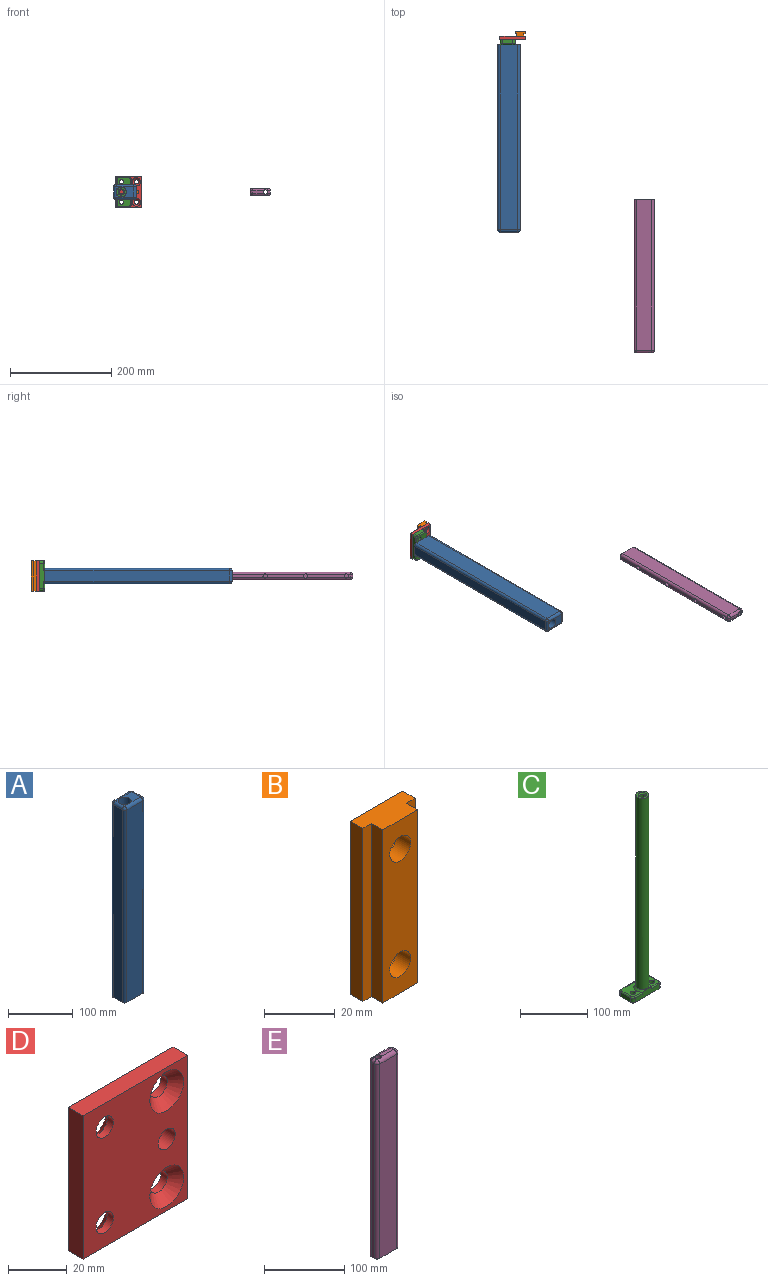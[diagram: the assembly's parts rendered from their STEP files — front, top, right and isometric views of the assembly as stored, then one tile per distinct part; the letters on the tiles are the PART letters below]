
ASSEMBLY  parts=5 mates=9
PART A: 32 faces, bbox 45x30x370 mm
  f0: plane 8.58x8.58mm, normal (0,0,1), area 20.1mm2, adj f6,f27,f31
  f1: plane 8.58x8.58mm, normal (0,0,1), area 20.1mm2, adj f6,f28,f31
  f2: plane 365x20mm, normal (-1,0,0), area 7300mm2, adj f8,f9,f12,f31
  f3: plane 365x35mm, normal (0,-1,0), area 12775mm2, adj f8,f9,f10,f27
  f4: plane 365x20mm, normal (1,0,0), area 7022.9mm2, adj f8,f10,f11,f13,f15,f17,f19,f21
  f5: plane 365x35mm, normal (0,1,0), area 12775mm2, adj f8,f11,f12,f28
  f6: cylinder r=10.1mm len=363mm, axis (0,0,-1), area 23036mm2, adj f0,f1,f7,f23,f27,f28,f31
  f7: plane 23.58x20mm, normal (0,0,1), area 340mm2, adj f6,f24,f27,f28
  f8: plane 45x30mm, normal (0,0,-1), area 868.6mm2, adj f2,f3,f4,f5,f9,f10,f11,f12
  f9: cylinder r=5mm len=365mm, axis (0,0,1), area 2866.7mm2, adj f2,f3,f8,f29
  f10: cylinder r=5mm len=365mm, axis (0,0,-1), area 2866.7mm2, adj f3,f4,f8,f25
  f11: cylinder r=5mm len=365mm, axis (0,0,1), area 2866.7mm2, adj f4,f5,f8,f26
  f12: cylinder r=5mm len=365mm, axis (0,0,-1), area 2866.7mm2, adj f2,f5,f8,f30
  f13: cylinder r=4.2mm len=15mm, axis (1,0,0), area 395.8mm2, adj f4,f14
  f14: plane 8.4x8.4mm, normal (1,0,0), area 55.4mm2, adj f13
  f15: cylinder r=4.2mm len=15mm, axis (1,0,0), area 395.8mm2, adj f4,f16
  f16: plane 8.4x8.4mm, normal (1,0,0), area 55.4mm2, adj f15
  f17: cylinder r=4.2mm len=15mm, axis (1,0,0), area 395.8mm2, adj f4,f18
  f18: plane 8.4x8.4mm, normal (1,0,0), area 55.4mm2, adj f17
  f19: cylinder r=4.2mm len=15mm, axis (1,0,0), area 395.8mm2, adj f4,f20
  f20: plane 8.4x8.4mm, normal (1,0,0), area 55.4mm2, adj f19
  f21: cylinder r=4.2mm len=15mm, axis (1,0,0), area 395.8mm2, adj f4,f22
  f22: plane 8.4x8.4mm, normal (1,0,0), area 55.4mm2, adj f21
  f23: cone r=12.1mm half-angle=15.9deg, axis (0,0,-1), area 507.7mm2, adj f6,f8
  f24: cylinder r=5mm len=20mm, axis (0,-1,0), area 157.1mm2, adj f4,f7,f25,f26
  f25: sphere r=5mm, area 39.3mm2, adj f10,f24,f27
  f26: sphere r=5mm, area 39.3mm2, adj f11,f24,f28
  f27: cylinder r=5mm len=35mm, axis (-1,0,0), area 274.7mm2, adj f0,f3,f6,f7,f25,f29
  f28: cylinder r=5mm len=35mm, axis (1,0,0), area 274.7mm2, adj f1,f5,f6,f7,f26,f30
  f29: sphere r=5mm, area 39.3mm2, adj f9,f27,f31
  f30: sphere r=5mm, area 39.3mm2, adj f12,f28,f31
  f31: cylinder r=5mm len=20mm, axis (0,1,0), area 156.9mm2, adj f0,f1,f2,f6,f29,f30
PART B: 34 faces, bbox 21x9.5x60 mm
  f0: plane 60x14mm, normal (0,-1,0), area 729.2mm2, adj f2,f7,f8,f9,f32,f33
  f1: plane 60x21mm, normal (0,1,0), area 939.7mm2, adj f4,f5,f8,f9,f10,f11,f12,f13
  f2: plane 60x4.5mm, normal (1,0,0), area 270mm2, adj f0,f3,f8,f9
  f3: plane 60x3.5mm, normal (0,-1,0), area 210mm2, adj f2,f4,f8,f9
  f4: plane 60x5mm, normal (1,0,0), area 300mm2, adj f1,f3,f8,f9
  f5: plane 60x5mm, normal (-1,0,0), area 300mm2, adj f1,f6,f8,f9
  f6: plane 60x3.5mm, normal (0,-1,0), area 210mm2, adj f5,f7,f8,f9
  f7: plane 60x4.5mm, normal (-1,0,0), area 270mm2, adj f0,f6,f8,f9
  f8: plane 21x9.5mm, normal (0,0,1), area 168mm2, adj f0,f1,f2,f3,f4,f5,f6,f7
  f9: plane 21x9.5mm, normal (0,0,-1), area 168mm2, adj f0,f1,f2,f3,f4,f5,f6,f7
  f10: plane 6.7x4mm, normal (-0.5,0,-0.87), area 30.9mm2, adj f1,f11,f19,f20
  f11: plane 4x0.3mm, normal (0,0,-1), area 1.2mm2, adj f1,f10,f12,f20
  f12: plane 7.74x4mm, normal (-1,0,0), area 30.9mm2, adj f1,f11,f13,f20
  f13: plane 4x0.3mm, normal (0,0,1), area 1.2mm2, adj f1,f12,f14,f20
  f14: plane 6.7x4mm, normal (-0.5,0,0.87), area 30.9mm2, adj f1,f13,f15,f20
  f15: plane 6.7x4mm, normal (0.5,0,0.87), area 30.9mm2, adj f1,f14,f16,f20
  f16: plane 4x0.3mm, normal (0,0,1), area 1.2mm2, adj f1,f15,f17,f20
  f17: plane 7.74x4mm, normal (1,0,0), area 30.9mm2, adj f1,f16,f18,f20
  f18: plane 4x0.3mm, normal (0,0,-1), area 1.2mm2, adj f1,f17,f19,f20
  f19: plane 6.7x4mm, normal (0.5,0,-0.87), area 30.9mm2, adj f1,f10,f18,f20
  f20: plane 15.47x14mm, normal (0,1,0), area 104.7mm2, adj f10,f11,f12,f13,f14,f15,f16,f17
  f21: plane 4x0.3mm, normal (0,0,-1), area 1.2mm2, adj f1,f22,f30,f31
  f22: plane 6.7x4mm, normal (0.5,0,-0.87), area 30.9mm2, adj f1,f21,f23,f31
  f23: plane 6.7x4mm, normal (-0.5,0,-0.87), area 30.9mm2, adj f1,f22,f24,f31
  f24: plane 4x0.3mm, normal (0,0,-1), area 1.2mm2, adj f1,f23,f25,f31
  f25: plane 7.74x4mm, normal (-1,0,0), area 30.9mm2, adj f1,f24,f26,f31
  f26: plane 4x0.3mm, normal (0,0,1), area 1.2mm2, adj f1,f25,f27,f31
  f27: plane 6.7x4mm, normal (-0.5,0,0.87), area 30.9mm2, adj f1,f26,f28,f31
  f28: plane 6.7x4mm, normal (0.5,0,0.87), area 30.9mm2, adj f1,f27,f29,f31
  f29: plane 4x0.3mm, normal (0,0,1), area 1.2mm2, adj f1,f28,f30,f31
  f30: plane 7.74x4mm, normal (1,0,0), area 30.9mm2, adj f1,f21,f29,f31
  f31: plane 15.47x14mm, normal (0,1,0), area 104.7mm2, adj f21,f22,f23,f24,f25,f26,f27,f28
  f32: cylinder r=4.2mm len=8.4mm, axis (0,1,0), area 145.1mm2, adj f0,f31
  f33: cylinder r=4.2mm len=8.4mm, axis (0,1,0), area 145.1mm2, adj f0,f20
PART C: 26 faces, bbox 60.8x35.1x360 mm
  f0: plane 56x26mm, normal (0,0,1), area 895.3mm2, adj f6,f7,f11,f17,f18,f19,f20,f21
  f1: plane 60x30mm, normal (0,0,-1), area 1612.3mm2, adj f2,f3,f4,f5,f6,f7,f10,f13
  f2: plane 20x8mm, normal (-1,0,0), area 160mm2, adj f1,f13,f16,f21
  f3: plane 50x12.71mm, normal (0,-1,0), area 464.9mm2, adj f1,f11,f13,f14,f17,f18
  f4: plane 20x8mm, normal (1,0,0), area 160mm2, adj f1,f14,f15,f22
  f5: plane 50x8mm, normal (0,1,0), area 400mm2, adj f1,f15,f16,f25
  f6: cylinder r=4.2mm len=10mm, axis (0,0,1), area 263.9mm2, adj f0,f1
  f7: cylinder r=4.2mm len=10mm, axis (0,0,1), area 263.9mm2, adj f0,f1
  f8: cylinder r=9.7mm len=347mm, axis (0,0,-1), area 21148.6mm2, adj f9,f11
  f9: plane 19.4x19.4mm, normal (0,0,1), area 174.8mm2, adj f8,f12
  f10: cylinder r=4.2mm len=358mm, axis (0,0,1), area 9447.4mm2, adj f1,f12
  f11: cone r=9.7mm half-angle=45deg, axis (0,0,-1), area 261.3mm2, adj f0,f3,f8,f17,f18
  f12: cone r=4.2mm half-angle=45deg, axis (0,0,1), area 92.4mm2, adj f9,f10
  f13: cylinder r=5mm len=8mm, axis (0,0,1), area 62.8mm2, adj f1,f2,f3,f19
  f14: cylinder r=5mm len=8mm, axis (0,0,-1), area 62.8mm2, adj f1,f3,f4,f20
  f15: cylinder r=5mm len=8mm, axis (0,0,1), area 62.8mm2, adj f1,f4,f5,f24
  f16: cylinder r=5mm len=8mm, axis (0,0,-1), area 62.8mm2, adj f1,f2,f5,f23
  f17: cylinder r=2mm len=15.68mm, axis (-1,0,0), area 48.1mm2, adj f0,f3,f11,f19
  f18: cylinder r=2mm len=15.68mm, axis (-1,0,0), area 48.1mm2, adj f0,f3,f11,f20
  f19: torus R=3mm, axis (0,0,1), area 21.1mm2, adj f0,f13,f17,f21
  f20: torus R=3mm, axis (0,0,1), area 21.1mm2, adj f0,f14,f18,f22
  f21: cylinder r=2mm len=20mm, axis (0,1,0), area 62.8mm2, adj f0,f2,f19,f23
  f22: cylinder r=2mm len=20mm, axis (0,-1,0), area 62.8mm2, adj f0,f4,f20,f24
  f23: torus R=3mm, axis (0,0,1), area 21.1mm2, adj f0,f16,f21,f25
  f24: torus R=3mm, axis (0,0,1), area 21.1mm2, adj f0,f15,f22,f25
  f25: cylinder r=2mm len=50mm, axis (1,0,0), area 157.1mm2, adj f0,f5,f23,f24
PART D: 15 faces, bbox 50.5x7x60 mm
  f0: plane 60x50.5mm, normal (0,-1,0), area 2443.9mm2, adj f2,f3,f4,f5,f6,f9,f12,f13
  f1: plane 60x50.5mm, normal (0,1,0), area 2443.9mm2, adj f2,f3,f4,f7,f8,f9,f10,f11
  f2: plane 60x7mm, normal (-1,0,0), area 420mm2, adj f0,f1,f3,f4
  f3: plane 50.5x7mm, normal (0,0,1), area 353.5mm2, adj f0,f1,f2,f9
  f4: plane 50.5x7mm, normal (0,0,-1), area 353.5mm2, adj f0,f1,f2,f9
  f5: cylinder r=4.2mm len=8.4mm, axis (0,1,0), area 79.2mm2, adj f0,f8
  f6: cylinder r=4.2mm len=8.4mm, axis (0,1,0), area 79.2mm2, adj f0,f7
  f7: cone r=4.2mm half-angle=45deg, axis (0,1,0), area 220.4mm2, adj f1,f6
  f8: cone r=8.2mm half-angle=45deg, axis (0,1,0), area 220.4mm2, adj f1,f5
  f9: plane 60x7mm, normal (1,0,0), area 420mm2, adj f0,f1,f3,f4
  f10: cylinder r=4.2mm len=8.4mm, axis (0,-1,0), area 79.2mm2, adj f1,f12
  f11: cylinder r=4.2mm len=8.4mm, axis (0,-1,0), area 79.2mm2, adj f1,f13
  f12: cone r=8.2mm half-angle=45deg, axis (0,-1,0), area 220.4mm2, adj f0,f10
  f13: cone r=4.2mm half-angle=45deg, axis (0,-1,0), area 220.4mm2, adj f0,f11
  f14: cylinder r=4.1mm len=8.2mm, axis (0,1,0), area 180.3mm2, adj f0,f1
PART E: 32 faces, bbox 40x15x302 mm
  f0: plane 21.63x5mm, normal (0,0,1), area 105.3mm2, adj f9,f25,f26,f30
  f1: plane 73.25x5mm, normal (1,0,0), area 360.6mm2, adj f13,f14,f20,f22
  f2: plane 45.83x5mm, normal (1,0,0), area 226.3mm2, adj f11,f13,f14,f22
  f3: plane 73.25x5mm, normal (1,0,0), area 360.6mm2, adj f13,f14,f18,f20
  f4: plane 73.25x5mm, normal (1,0,0), area 360.6mm2, adj f13,f14,f16,f18
  f5: plane 5x4.43mm, normal (1,0,0), area 19.3mm2, adj f13,f14,f16,f26
  f6: plane 297x5mm, normal (-1,0,0), area 1485mm2, adj f11,f12,f15,f29
  f7: plane 297x30mm, normal (0,-1,0), area 8910mm2, adj f11,f12,f13,f30
  f8: plane 297x30mm, normal (0,1,0), area 8910mm2, adj f11,f14,f15,f25
  f9: cylinder r=4.2mm len=302mm, axis (0,0,-1), area 7967.2mm2, adj f0,f10,f11,f25,f30
  f10: plane 5x1.63mm, normal (0,0,1), area 5.3mm2, adj f9,f25,f29,f30
  f11: plane 40x15mm, normal (0,0,-1), area 523.1mm2, adj f2,f6,f7,f8,f9,f12,f13,f14
  f12: cylinder r=5mm len=297mm, axis (0,0,1), area 2332.6mm2, adj f6,f7,f11,f31
  f13: cylinder r=5mm len=297mm, axis (0,0,-1), area 2300.1mm2, adj f1,f2,f3,f4,f5,f7,f11,f16
  f14: cylinder r=5mm len=297mm, axis (0,0,1), area 2300.1mm2, adj f1,f2,f3,f4,f5,f8,f11,f16
  f15: cylinder r=5mm len=297mm, axis (0,0,-1), area 2332.6mm2, adj f6,f8,f11,f27
  f16: cylinder r=4.2mm len=25mm, axis (1,0,0), area 657.3mm2, adj f4,f5,f13,f14,f17
  f17: plane 8.4x8.4mm, normal (1,0,0), area 55.4mm2, adj f16
  f18: cylinder r=4.2mm len=25mm, axis (1,0,0), area 657.3mm2, adj f3,f4,f13,f14,f19
  f19: plane 8.4x8.4mm, normal (1,0,0), area 55.4mm2, adj f18
  f20: cylinder r=4.2mm len=25mm, axis (1,0,0), area 657.3mm2, adj f1,f3,f13,f14,f21
  f21: plane 8.4x8.4mm, normal (1,0,0), area 55.4mm2, adj f20
  f22: cylinder r=4.2mm len=25mm, axis (1,0,0), area 657.3mm2, adj f1,f2,f13,f14,f23
  f23: plane 8.4x8.4mm, normal (1,0,0), area 55.4mm2, adj f22
  f24: sphere r=5mm, area 39.3mm2, adj f14,f25,f26
  f25: cylinder r=5mm len=30mm, axis (1,0,0), area 227.5mm2, adj f0,f8,f9,f10,f24,f27
  f26: cylinder r=5mm len=5mm, axis (0,-1,0), area 39.3mm2, adj f0,f5,f24,f28
  f27: sphere r=5mm, area 39.3mm2, adj f15,f25,f29
  f28: sphere r=5mm, area 39.3mm2, adj f13,f26,f30
  f29: cylinder r=5mm len=5mm, axis (0,1,0), area 39.3mm2, adj f6,f10,f27,f31
  f30: cylinder r=5mm len=30mm, axis (-1,0,0), area 227.5mm2, adj f0,f7,f9,f10,f28,f31
  f31: sphere r=5mm, area 39.3mm2, adj f12,f29,f30
PLACE A rot(axis=(1,0,0),90deg) t=(159.25,236.73,29.16)mm
PLACE B t=(204.25,253.73,14.16)mm
PLACE C rot(axis=(0.58,0.58,-0.58),120deg) t=(164.25,246.73,74.16)mm
PLACE D t=(174.25,246.73,14.16)mm
PLACE E rot(axis=(0,-0.71,0.71),180deg) t=(468.75,-69.07,51.66)mm
MATE cylindrical A.f6 <-> C.f8  axis (0,1,0) through (174.25,-133.27,44.16)mm
MATE parallel A.f8 <-> C.f0  axis (0,1,0) through (185.72,236.73,44.16)mm
MATE parallel A.f7 <-> E.f10  axis (0,-1,0) through (190.62,-133.27,44.16)mm
MATE slider E.f22 <-> A.f21  axis (-1,0,0) through (441.25,-118.27,44.16)mm
MATE cylindrical C.f7 <-> D.f5  axis (0,-1,0) through (174.25,236.73,64.16)mm
MATE planar B.f0 <-> D.f1  axis (0,-1,0) through (204.25,253.73,44.16)mm
MATE cylindrical D.f11 <-> B.f33  axis (0,-1,0) through (204.25,252.23,64.16)mm
MATE planar C.f1 <-> D.f0  axis (0,1,0) through (179.77,246.73,44.16)mm
MATE cylindrical C.f6 <-> D.f6  axis (0,-1,0) through (174.25,236.73,24.16)mm
